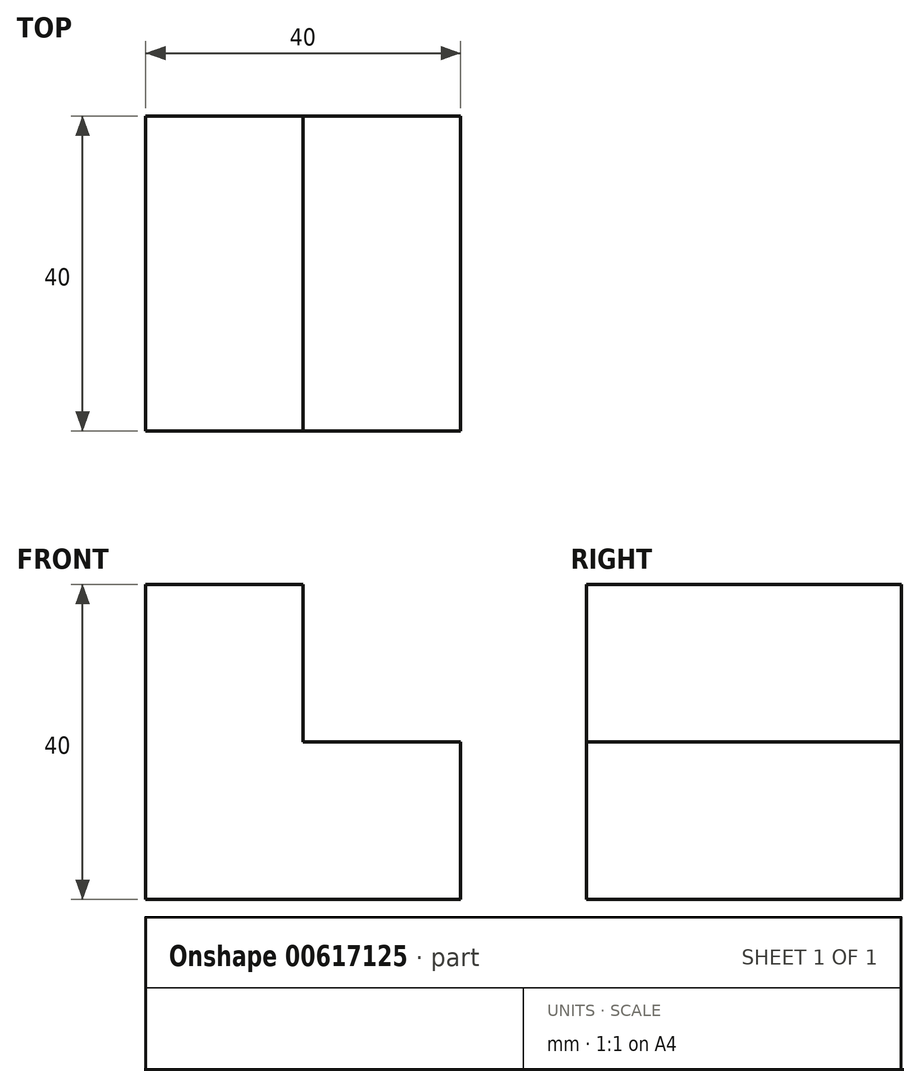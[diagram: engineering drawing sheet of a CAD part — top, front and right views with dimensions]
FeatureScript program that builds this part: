
annotation { "Feature Type Name" : "Feature", "Feature Type Description" : "" }
export const myFeature = defineFeature(function(context is Context, id is Id, definition is map)
    precondition{}
    {
        {
            var Q0;
            Q0=qCreatedBy(makeId("Front.planeOp"),FACE);
            var sketch = newSketch(context, id + "F0", { "sketchPlane" : qUnion([Q0])});
            skLineSegment(sketch, "E0", {"start": v(-25.76, 20) * mm, "end": v(-5.76, 20) * mm});
            skLineSegment(sketch, "E1", {"start": v(-5.76, 20) * mm, "end": v(-5.76, 0) * mm});
            skLineSegment(sketch, "E2", {"start": v(-5.76, 0) * mm, "end": v(14.24, 0) * mm});
            skLineSegment(sketch, "E3", {"start": v(14.24, -20) * mm, "end": v(-25.76, -20) * mm});
            skLineSegment(sketch, "E4", {"start": v(-25.76, 20) * mm, "end": v(-25.76, -20) * mm});
            skLineSegment(sketch, "E5", {"start": v(14.24, 0) * mm, "end": v(14.24, -20) * mm});
            skSolve(sketch);
        }
        {
            var Q0;
            Q0 = qSketchRegion(id + "F0", true);
            extrude(context, id + "F1", {"entities" : qUnion([Q0]), "depth" : 40 * mm, "offsetDistance" : 25 * mm});
        }
    });
